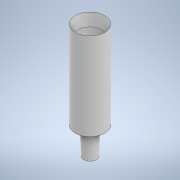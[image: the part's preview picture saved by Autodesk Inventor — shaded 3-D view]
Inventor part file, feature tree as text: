
AUTODESK INVENTOR PART (.ipt)
format: ipt  version: 2020 (Build 240168000, 168)  size: 114,688 bytes
history: native  units: in
note: dims shown in document units (in); Inventor stores cm internally (conversion verified against a paired STEP export)
features: revolve x1, sketch x1
ambient origin geometry x8: Origin, YZ Plane, XZ Plane, XY Plane, X Axis, Y Axis, Z Axis, Center Point
bodies: Solid1 (feature_tree)
feature tree (2):
  revolve  "Revolution1"  [1 undecoded]
  sketch  "Sketch1"  dims[d0=0.0787in d6=0.3346in d20=45.0deg d21=90.0deg]
note: 1 required parameter value undecoded (feature->parameter linkage not recoverable at this tier; creation-order binding heuristic only, values carry confidence <= 0.55)
